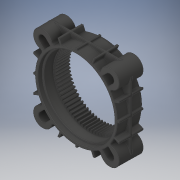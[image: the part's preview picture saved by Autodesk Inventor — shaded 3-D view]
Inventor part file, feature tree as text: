
AUTODESK INVENTOR PART (.ipt)
format: ipt  version: 2018 (Build 220112000, 112)  size: 1,938,432 bytes
history: native  units: in
note: dims shown in document units (in); Inventor stores cm internally (conversion verified against a paired STEP export)
features: fillet x1
ambient origin geometry x8: Origin, YZ Plane, XZ Plane, XY Plane, X Axis, Y Axis, Z Axis, Center Point
bodies: Solid1 (feature_tree)
feature tree (1):
  fillet  "Fillet12"  [1 undecoded]
note: 1 required parameter value undecoded (feature->parameter linkage not recoverable at this tier; creation-order binding heuristic only, values carry confidence <= 0.55)
